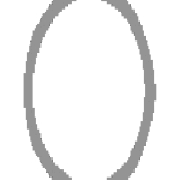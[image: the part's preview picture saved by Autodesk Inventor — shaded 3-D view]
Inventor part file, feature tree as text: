
AUTODESK INVENTOR PART (.ipt)
format: ipt  version: 2021 (Build 250183000, 183)  size: 110,080 bytes
history: native  units: in
note: dims shown in document units (in); Inventor stores cm internally (conversion verified against a paired STEP export)
features: other x4, sketch x3, plane x1
ambient origin geometry x8: Origin, YZ Plane, XZ Plane, XY Plane, X Axis, Y Axis, Z Axis, Center Point
bodies: Solid1 (feature_tree), Body (feature_tree)
feature tree (8):
  other  "Driven Length"
  other  "Frame Generator"
  other  "Start Plane"
  other  "End Plane"
  sketch  "Sketch"  dims[d2=14.625in d4=-0.0in d5=14.625in d6=0.12in d7=0.0in d8=90.0deg d9=14.625in]
  sketch  "Sketch2"  dims[d0=1.0in]
  plane  "Work Plane3"
  sketch  "Sketch3"  dims[d1=0.065in]
